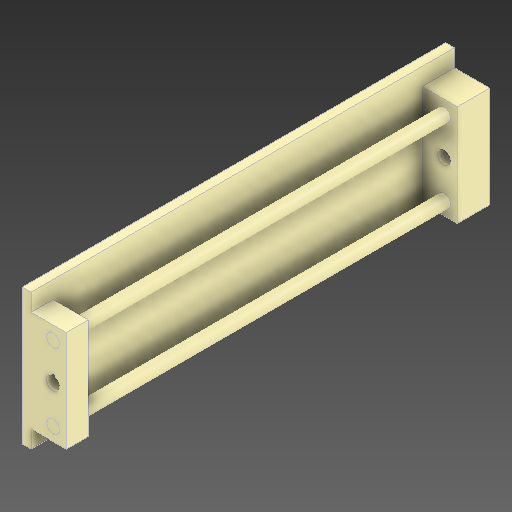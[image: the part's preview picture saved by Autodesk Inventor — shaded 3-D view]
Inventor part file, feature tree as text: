
AUTODESK INVENTOR PART (.ipt)
format: ipt  version: 2020 (Build 240168000, 168)  size: 214,016 bytes
history: native  units: mm
features: other x10, extrude x1, sketch x1, projected_geometry x1
ambient origin geometry x8: Origin, YZ Plane, XZ Plane, XY Plane, X Axis, Y Axis, Z Axis, Center Point
bodies: Body1 (feature_tree)
feature tree (13):
  other  "Bearing2.ipt"
  extrude  "擠出1"  Depth=110.0mm
  other  "直接編輯1"
  other  "直接編輯2"
  other  "直接編輯3"
  other  "實體1::Bearing2.ipt"
  other  "標籤特徵1"
  sketch  "草圖1"
  projected_geometry  "投影迴路1"
  other  "實體1"
  other  "移動1"
  other  "移動2"
  other  "移動3"
